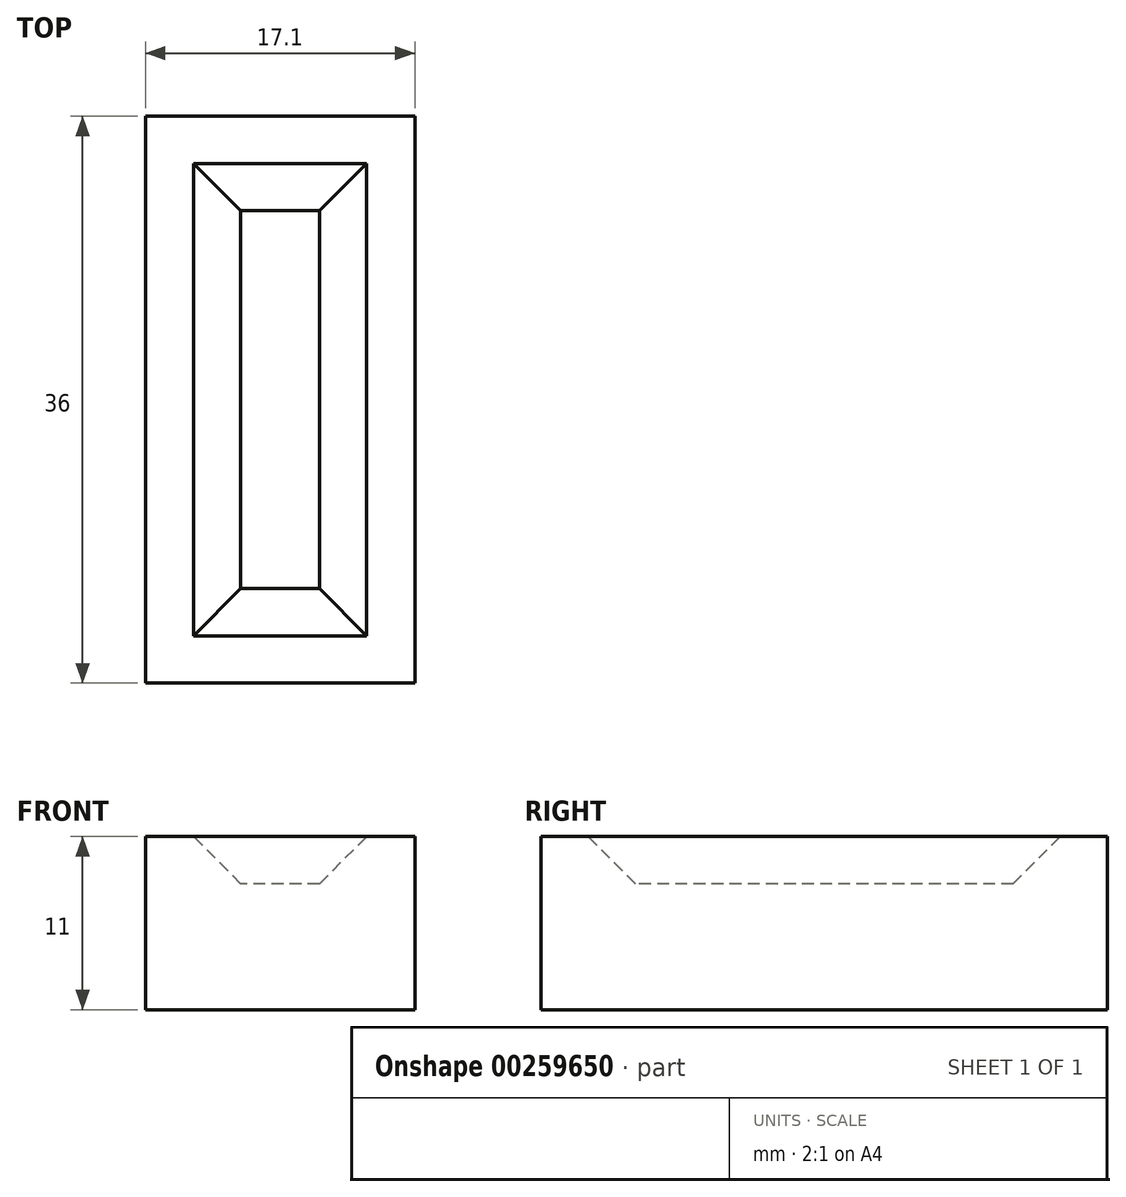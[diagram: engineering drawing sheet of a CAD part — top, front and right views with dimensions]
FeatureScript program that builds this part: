
annotation { "Feature Type Name" : "Feature", "Feature Type Description" : "" }
export const myFeature = defineFeature(function(context is Context, id is Id, definition is map)
    precondition{}
    {
        {
            var Q0;
            Q0=qCreatedBy(makeId("Top.planeOp"),FACE);
            var sketch = newSketch(context, id + "F3", { "sketchPlane" : qUnion([Q0])});
            skLineSegment(sketch, "E0.bottom", {"start": v(-8.55, 18) * mm, "end": v(8.55, 18) * mm});
            skLineSegment(sketch, "E0.top", {"start": v(-8.55, -18) * mm, "end": v(8.55, -18) * mm});
            skLineSegment(sketch, "E0.left", {"start": v(-8.55, 18) * mm, "end": v(-8.55, -18) * mm});
            skLineSegment(sketch, "E0.right", {"start": v(8.55, 18) * mm, "end": v(8.55, -18) * mm});
            skPoint(sketch, "E0.middle", {"position": v(0, 0) * mm});
            skSolve(sketch);
        }
        {
            var Q0;
            Q0 = qSketchRegion(id + "F3", true);
            extrude(context, id + "F0", {"entities" : qUnion([Q0]), "endBound" : BoundingType.SYMMETRIC, "depth" : 11 * mm});
        }
        {
            var Q0;
            Q0=qCreatedBy(makeId("Right.planeOp"),FACE);
            var sketch = newSketch(context, id + "F4", { "sketchPlane" : qUnion([Q0])});
            skLineSegment(sketch, "E1", {"start": v(-15, 5.5) * mm, "end": v(15, 5.5) * mm});
            skLineSegment(sketch, "E2.0", {"start": v(-15, 2.5) * mm, "end": v(-15, 5.5) * mm});
            skLineSegment(sketch, "E3.0", {"start": v(15, 2.5) * mm, "end": v(15, 5.5) * mm});
            skLineSegment(sketch, "E4.0", {"start": v(-15, 2.5) * mm, "end": v(15, 2.5) * mm});
            skPoint(sketch, "E5.orphan", {"position": v(18, 5.5) * mm});
            skPoint(sketch, "E6.orphan", {"position": v(-18, 5.5) * mm});
            skPoint(sketch, "E7.orphan", {"position": v(0, 5.5) * mm});
            skSolve(sketch);
        }
        {
            var Q0;
            Q0 = qSketchRegion(id + "F4", true);
            extrude(context, id + "F1", {"entities" : qUnion([Q0]), "operationType" : NewBodyOperationType.REMOVE, "endBound" : BoundingType.SYMMETRIC, "depth" : 11 * mm});
        }
        {
            var Q0;
            Q0=makeQuery(id+"F1.boolean.opBoolean","COPY",EDGE,{"derivedFrom":makeQuery(id+"F1.opExtrude","CAP_EDGE",EDGE,{"disambiguationData":[OSD([sQuery(id+"F4.wireOp",EDGE,"E4.0")])],"isStart":true})});
            var Q1;
            Q1=makeQuery(id+"F1.boolean.opBoolean","COPY",EDGE,{"derivedFrom":makeQuery(id+"F1.opExtrude","SWEPT_EDGE",EDGE,{"disambiguationData":[OSD([sQuery(id+"F4.wireOp",EDGE,"E2.0"),sQuery(id+"F4.wireOp",EDGE,"E4.0")])]})});
            var Q2;
            Q2=makeQuery(id+"F1.boolean.opBoolean","COPY",EDGE,{"derivedFrom":makeQuery(id+"F1.opExtrude","SWEPT_EDGE",EDGE,{"disambiguationData":[OSD([sQuery(id+"F4.wireOp",EDGE,"E3.0"),sQuery(id+"F4.wireOp",EDGE,"E4.0")])]})});
            var Q3;
            Q3=makeQuery(id+"F1.boolean.opBoolean","COPY",EDGE,{"derivedFrom":makeQuery(id+"F1.opExtrude","CAP_EDGE",EDGE,{"disambiguationData":[OSD([sQuery(id+"F4.wireOp",EDGE,"E4.0")])],"isStart":false})});
            chamfer(context, id + "F2", {"entities" : qUnion([Q0, Q1, Q2, Q3]), "width" : 3 * mm, "tangentPropagation" : true});
        }
    });
